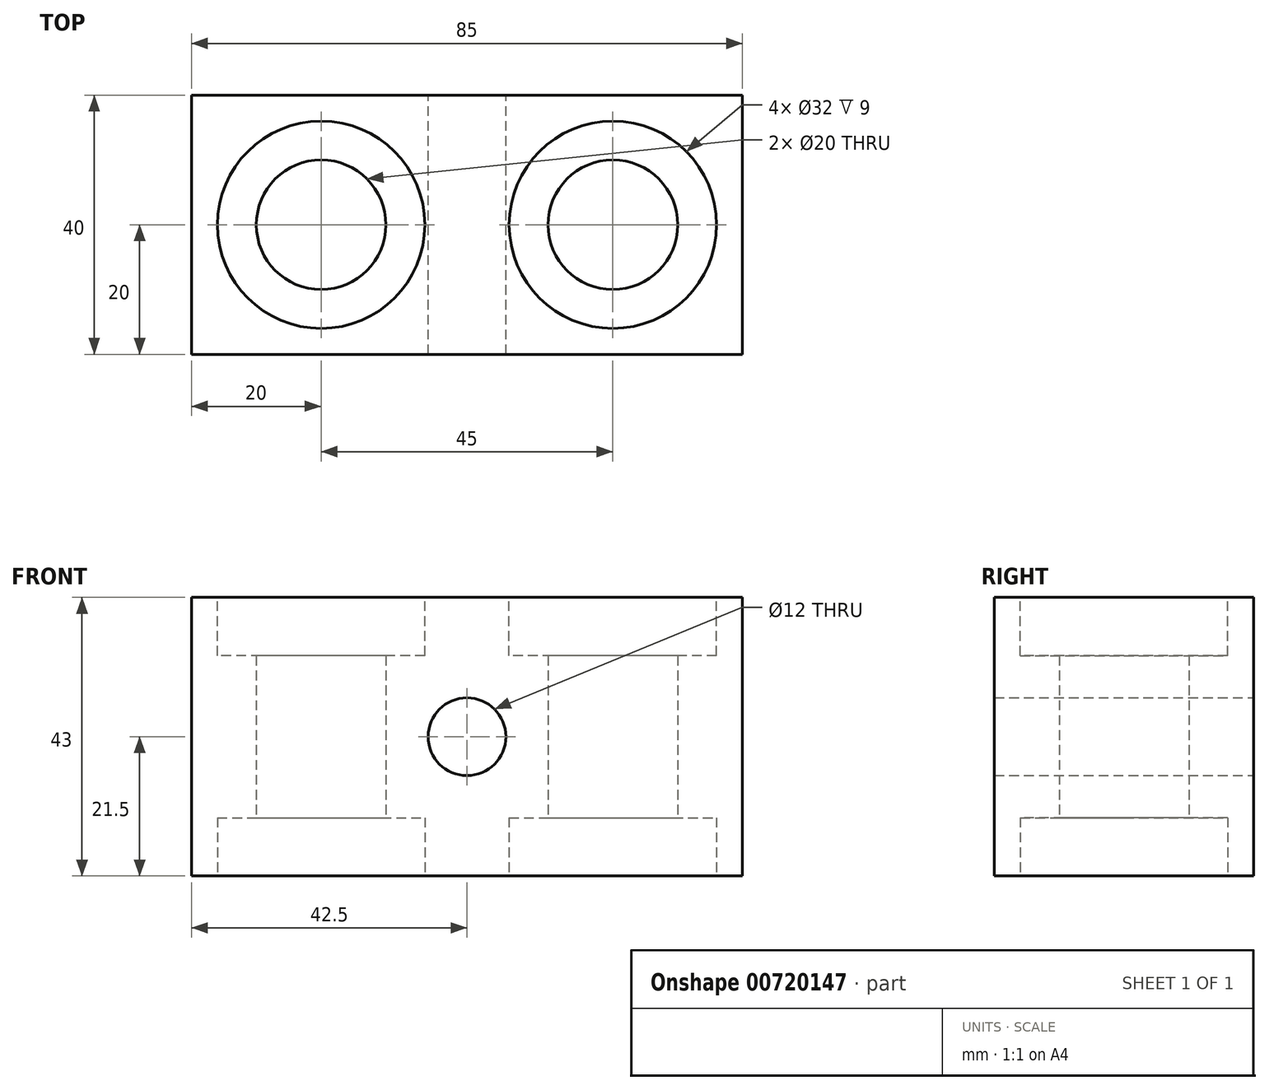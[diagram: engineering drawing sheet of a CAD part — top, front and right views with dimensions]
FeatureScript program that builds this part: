
annotation { "Feature Type Name" : "Feature", "Feature Type Description" : "" }
export const myFeature = defineFeature(function(context is Context, id is Id, definition is map)
    precondition{}
    {
        {
            var Q0;
            Q0=qCreatedBy(makeId("Front.planeOp"),FACE);
            var sketch = newSketch(context, id + "F0", { "sketchPlane" : qUnion([Q0])});
            skLineSegment(sketch, "E0.bottom", {"start": v(0, 0) * mm, "end": v(85, 0) * mm});
            skLineSegment(sketch, "E0.top", {"start": v(0, 43) * mm, "end": v(85, 43) * mm});
            skLineSegment(sketch, "E0.left", {"start": v(0, 0) * mm, "end": v(0, 43) * mm});
            skLineSegment(sketch, "E0.right", {"start": v(85, 0) * mm, "end": v(85, 43) * mm});
            skCircle(sketch, "E1", {"center": v(42.5, 21.5) * mm, "radius": 6 * mm});
            skPoint(sketch, "E1.centerSnap0", {"position": v(0, 21.5) * mm});
            skPoint(sketch, "E1.centerSnap1", {"position": v(42.5, 43) * mm});
            skSolve(sketch);
        }
        {
            var Q0;
            Q0=makeQuery(id+"F0.imprint","IMPRINT",FACE,{"disambiguationData":[TD([[makeQuery(id+"F0.imprint","IMPRINT",EDGE,{"derivedFrom":sQuery(id+"F0.wireOp",EDGE,"E0.bottom")}),1.0]])]});
            extrude(context, id + "F1", {"entities" : qUnion([Q0]), "depth" : 40 * mm, "offsetDistance" : 25 * mm});
        }
        {
            var Q0;
            Q0=makeQuery(id+"F1.opExtrude","SWEPT_FACE",FACE,{"disambiguationData":[OSD([sQuery(id+"F0.wireOp",EDGE,"E0.bottom")])]});
            var sketch = newSketch(context, id + "F2", { "sketchPlane" : qUnion([Q0])});
            skCircle(sketch, "E2", {"center": v(20, 20) * mm, "radius": 10 * mm});
            skPoint(sketch, "E2.centerSnap0", {"position": v(0, 20) * mm});
            skCircle(sketch, "E3", {"center": v(65, 20) * mm, "radius": 10 * mm});
            skSolve(sketch);
        }
        {
            var Q0;
            Q0=makeQuery(id+"F2.imprint","IMPRINT",FACE,{"disambiguationData":[TD([[makeQuery(id+"F2.imprint","IMPRINT",EDGE,{"derivedFrom":sQuery(id+"F2.wireOp",EDGE,"E2")}),1.0]])]});
            var Q1;
            Q1=makeQuery(id+"F2.imprint","IMPRINT",FACE,{"disambiguationData":[TD([[makeQuery(id+"F2.imprint","IMPRINT",EDGE,{"derivedFrom":sQuery(id+"F2.wireOp",EDGE,"E3")}),1.0]])]});
            extrude(context, id + "F3", {"entities" : qUnion([Q0, Q1]), "operationType" : NewBodyOperationType.REMOVE, "endBound" : BoundingType.THROUGH_ALL, "oppositeDirection" : true, "depth" : 25 * mm, "offsetDistance" : 25 * mm});
        }
        {
            var Q0;
            Q0=makeQuery(id+"F1.opExtrude","SWEPT_FACE",FACE,{"disambiguationData":[OSD([sQuery(id+"F0.wireOp",EDGE,"E0.bottom")])]});
            var sketch = newSketch(context, id + "F4", { "sketchPlane" : qUnion([Q0])});
            skCircle(sketch, "E4", {"center": v(20, 20) * mm, "radius": 16 * mm});
            skCircle(sketch, "E5", {"center": v(65, 20) * mm, "radius": 16 * mm});
            skSolve(sketch);
        }
        {
            var Q0;
            Q0=makeQuery(id+"F4.imprint","IMPRINT",FACE,{"disambiguationData":[TD([[makeQuery(id+"F4.imprint","IMPRINT",EDGE,{"derivedFrom":sQuery(id+"F4.wireOp",EDGE,"E4")}),1.0]])]});
            var Q1;
            Q1=makeQuery(id+"F4.imprint","IMPRINT",FACE,{"disambiguationData":[TD([[makeQuery(id+"F4.imprint","IMPRINT",EDGE,{"derivedFrom":sQuery(id+"F4.wireOp",EDGE,"E5")}),1.0]])]});
            extrude(context, id + "F5", {"entities" : qUnion([Q0, Q1]), "operationType" : NewBodyOperationType.REMOVE, "oppositeDirection" : true, "depth" : 9 * mm, "offsetDistance" : 25 * mm});
        }
        {
            var Q0;
            Q0=makeQuery(id+"F1.opExtrude","SWEPT_FACE",FACE,{"disambiguationData":[OSD([sQuery(id+"F0.wireOp",EDGE,"E0.top")])]});
            var sketch = newSketch(context, id + "F6", { "sketchPlane" : qUnion([Q0])});
            skCircle(sketch, "E6", {"center": v(20, -20) * mm, "radius": 16 * mm});
            skCircle(sketch, "E7", {"center": v(65, -20) * mm, "radius": 16 * mm});
            skSolve(sketch);
        }
        {
            var Q0;
            Q0=makeQuery(id+"F6.imprint","IMPRINT",FACE,{"disambiguationData":[TD([[makeQuery(id+"F6.imprint","IMPRINT",EDGE,{"derivedFrom":sQuery(id+"F6.wireOp",EDGE,"E6")}),1.0]])]});
            var Q1;
            Q1=makeQuery(id+"F6.imprint","IMPRINT",FACE,{"disambiguationData":[TD([[makeQuery(id+"F6.imprint","IMPRINT",EDGE,{"derivedFrom":sQuery(id+"F6.wireOp",EDGE,"E7")}),1.0]])]});
            extrude(context, id + "F7", {"entities" : qUnion([Q0, Q1]), "operationType" : NewBodyOperationType.REMOVE, "oppositeDirection" : true, "depth" : 9 * mm, "offsetDistance" : 25 * mm});
        }
    });
